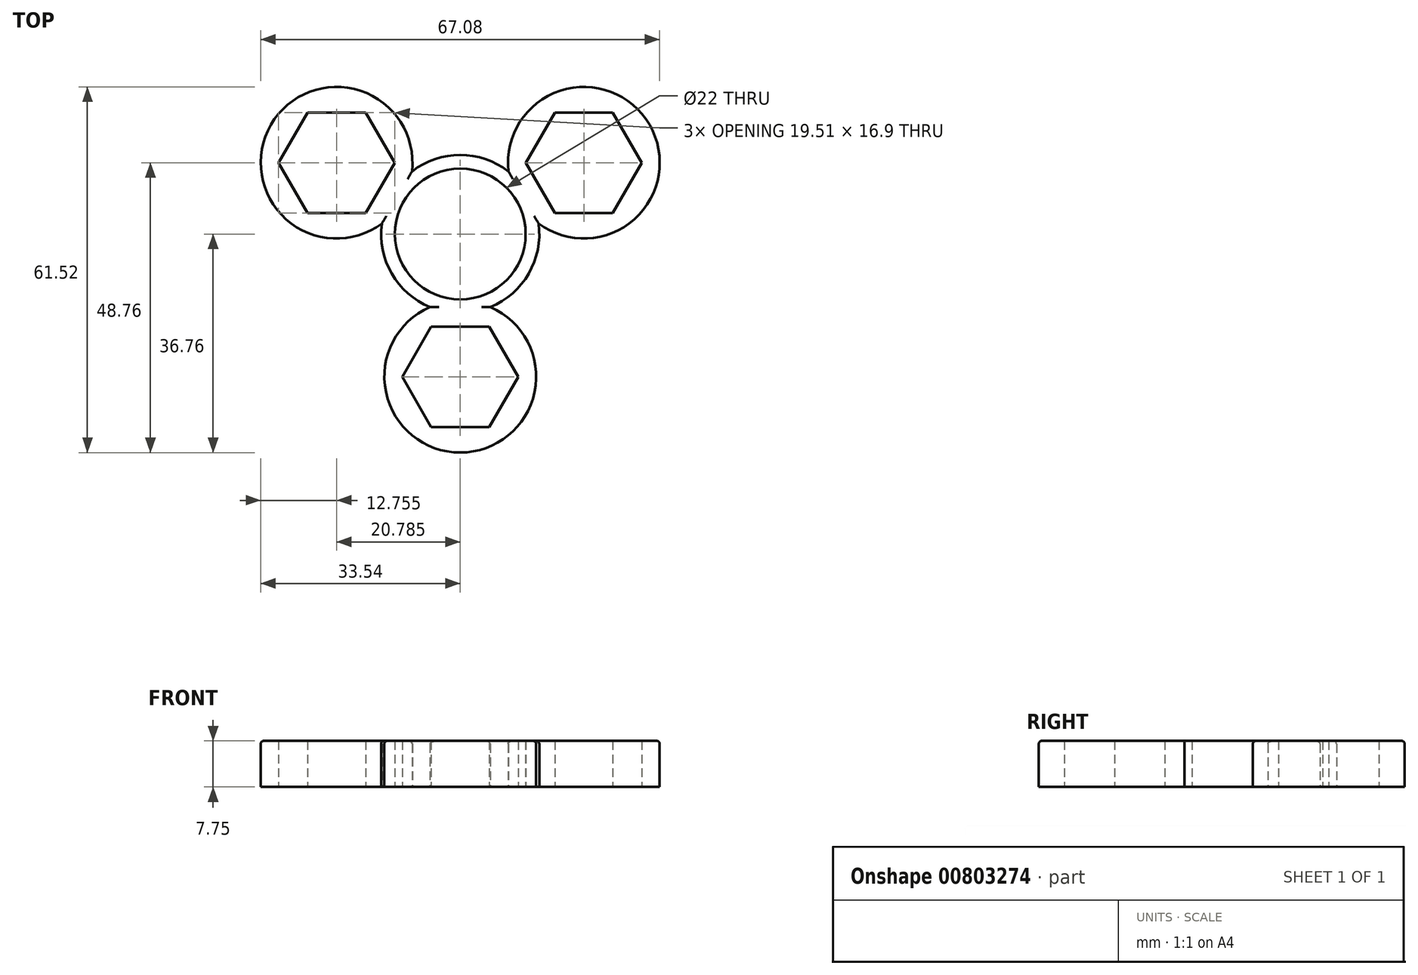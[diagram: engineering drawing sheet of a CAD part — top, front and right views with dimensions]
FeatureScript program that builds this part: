
annotation { "Feature Type Name" : "Feature", "Feature Type Description" : "" }
export const myFeature = defineFeature(function(context is Context, id is Id, definition is map)
    precondition{}
    {
        {
            var Q0;
            Q0=qCreatedBy(makeId("Top.planeOp"),FACE);
            var sketch = newSketch(context, id + "F0", { "sketchPlane" : qUnion([Q0])});
            skCircle(sketch, "E0", {"center": v(0, 0) * mm, "radius": 13.3 * mm});
            skCircle(sketch, "E1", {"center": v(0, -24) * mm, "radius": 12.76 * mm});
            skCircle(sketch, "E2", {"center": v(20.78, 12) * mm, "radius": 12.76 * mm});
            skCircle(sketch, "E3", {"center": v(-20.78, 12) * mm, "radius": 12.76 * mm});
            skLineSegment(sketch, "E4", {"start": v(-48.98, 58.94) * mm, "end": v(-57.64, 53.94) * mm, "construction": true});
            skLineSegment(sketch, "E5", {"start": v(-48.98, 58.94) * mm, "end": v(-48.98, 68.94) * mm, "construction": true});
            skLineSegment(sketch, "E6", {"start": v(-48.98, 58.94) * mm, "end": v(-40.32, 53.94) * mm, "construction": true});
            skCircle(sketch, "E7", {"center": v(-40.32, 53.94) * mm, "radius": 2.5 * mm});
            skCircle(sketch, "E8", {"center": v(-57.64, 53.94) * mm, "radius": 2.5 * mm});
            skCircle(sketch, "E9", {"center": v(-48.98, 68.94) * mm, "radius": 2.5 * mm});
            skCircle(sketch, "E10.cCircle", {"center": v(-48.98, 68.94) * mm, "radius": 1.68 * mm, "construction": true});
            skLineSegment(sketch, "E10.0", {"start": v(-47.05, 68.82) * mm, "end": v(-48.12, 67.2) * mm});
            skLineSegment(sketch, "E10.1", {"start": v(-48.12, 67.2) * mm, "end": v(-50.05, 67.33) * mm});
            skLineSegment(sketch, "E10.2", {"start": v(-50.05, 67.33) * mm, "end": v(-50.91, 69.06) * mm});
            skLineSegment(sketch, "E10.3", {"start": v(-50.91, 69.06) * mm, "end": v(-49.84, 70.68) * mm});
            skLineSegment(sketch, "E10.4", {"start": v(-49.84, 70.68) * mm, "end": v(-47.9, 70.55) * mm});
            skLineSegment(sketch, "E10.5", {"start": v(-47.9, 70.55) * mm, "end": v(-47.05, 68.82) * mm});
            skPoint(sketch, "E10.0.midPoint", {"position": v(-47.58, 68.01) * mm});
            skLineSegment(sketch, "E11", {"start": v(-20.78, 12) * mm, "end": v(0, 0) * mm, "construction": true});
            skLineSegment(sketch, "E12", {"start": v(20.78, 12) * mm, "end": v(0, 0) * mm, "construction": true});
            skLineSegment(sketch, "E13", {"start": v(0, -24) * mm, "end": v(0, 0) * mm, "construction": true});
            skCircle(sketch, "E14.cCircle", {"center": v(-20.78, 12) * mm, "radius": 8.45 * mm, "construction": true});
            skLineSegment(sketch, "E14.0", {"start": v(-25.66, 20.45) * mm, "end": v(-15.9, 20.45) * mm});
            skLineSegment(sketch, "E14.1", {"start": v(-15.9, 20.45) * mm, "end": v(-11.03, 12) * mm});
            skLineSegment(sketch, "E14.2", {"start": v(-11.03, 12) * mm, "end": v(-15.9, 3.55) * mm});
            skLineSegment(sketch, "E14.3", {"start": v(-15.9, 3.55) * mm, "end": v(-25.66, 3.55) * mm});
            skLineSegment(sketch, "E14.4", {"start": v(-25.66, 3.55) * mm, "end": v(-30.54, 12) * mm});
            skLineSegment(sketch, "E14.5", {"start": v(-30.54, 12) * mm, "end": v(-25.66, 20.45) * mm});
            skPoint(sketch, "E14.0.midPoint", {"position": v(-20.78, 20.45) * mm});
            skLineSegment(sketch, "E15.1.0", {"start": v(4.88, -32.45) * mm, "end": v(-4.88, -32.45) * mm});
            skLineSegment(sketch, "E15.1.1", {"start": v(-4.88, -32.45) * mm, "end": v(-9.76, -24) * mm});
            skLineSegment(sketch, "E15.1.2", {"start": v(-9.76, -24) * mm, "end": v(-4.88, -15.55) * mm});
            skLineSegment(sketch, "E15.1.3", {"start": v(-4.88, -15.55) * mm, "end": v(4.88, -15.55) * mm});
            skLineSegment(sketch, "E15.1.4", {"start": v(4.88, -15.55) * mm, "end": v(9.76, -24) * mm});
            skLineSegment(sketch, "E15.1.5", {"start": v(9.76, -24) * mm, "end": v(4.88, -32.45) * mm});
            skLineSegment(sketch, "E15.2.0", {"start": v(25.66, 20.45) * mm, "end": v(30.54, 12) * mm});
            skLineSegment(sketch, "E15.2.1", {"start": v(30.54, 12) * mm, "end": v(25.66, 3.55) * mm});
            skLineSegment(sketch, "E15.2.2", {"start": v(25.66, 3.55) * mm, "end": v(15.9, 3.55) * mm});
            skLineSegment(sketch, "E15.2.3", {"start": v(15.9, 3.55) * mm, "end": v(11.03, 12) * mm});
            skLineSegment(sketch, "E15.2.4", {"start": v(11.03, 12) * mm, "end": v(15.9, 20.45) * mm});
            skLineSegment(sketch, "E15.2.5", {"start": v(15.9, 20.45) * mm, "end": v(25.66, 20.45) * mm});
            skCircle(sketch, "E16", {"center": v(0, 0) * mm, "radius": 11 * mm});
            skSolve(sketch);
        }
        {
            var Q0;
            Q0=makeQuery(id+"F0.imprint","IMPRINT",FACE,{"disambiguationData":[TD([[makeQuery(id+"F0.imprint","IMPRINT",EDGE,{"derivedFrom":sQuery(id+"F0.wireOp",EDGE,"E14.0")}),1.0]])]});
            var Q1;
            Q1=makeQuery(id+"F0.imprint","IMPRINT",FACE,{"disambiguationData":[TD([[makeQuery(id+"F0.imprint","IMPRINT",EDGE,{"derivedFrom":sQuery(id+"F0.wireOp",EDGE,"E15.2.0")}),1.0]])]});
            var Q2;
            Q2=makeQuery(id+"F0.imprint","IMPRINT",FACE,{"disambiguationData":[TD([[makeQuery(id+"F0.imprint","IMPRINT",EDGE,{"derivedFrom":sQuery(id+"F0.wireOp",EDGE,"E15.1.0")}),1.0]])]});
            var Q3;
            {var subQ0=sQuery(id+"F0.wireOp",EDGE,"E3");var subQ1=sQuery(id+"F0.wireOp",EDGE,"E0");var subQ2=makeQuery(id+"F0.imprint","INTERSECT",VERTEX,{"disambiguationData":[OD(0.0)],"derivedFrom":[subQ1,subQ0]});Q3=makeQuery(id+"F0.imprint","IMPRINT",FACE,{"disambiguationData":[TD([[makeQuery(id+"F0.imprint","IMPRINT",EDGE,{"disambiguationData":[TD([[subQ2,-1.0]])],"derivedFrom":subQ1}),1.0]])]});}
            var Q4;
            {var subQ0=sQuery(id+"F0.wireOp",EDGE,"E1");var subQ1=sQuery(id+"F0.wireOp",EDGE,"E0");var subQ2=makeQuery(id+"F0.imprint","INTERSECT",VERTEX,{"disambiguationData":[OD(0.0)],"derivedFrom":[subQ1,subQ0]});Q4=makeQuery(id+"F0.imprint","IMPRINT",FACE,{"disambiguationData":[TD([[makeQuery(id+"F0.imprint","IMPRINT",EDGE,{"disambiguationData":[TD([[subQ2,-1.0]])],"derivedFrom":subQ1}),1.0]])]});}
            var Q5;
            Q5=makeQuery(id+"F0.imprint","IMPRINT",FACE,{"disambiguationData":[TD([[makeQuery(id+"F0.imprint","IMPRINT",EDGE,{"derivedFrom":sQuery(id+"F0.wireOp",EDGE,"E16")}),-1.0]])]});
            var Q6;
            {var subQ0=sQuery(id+"F0.wireOp",EDGE,"E2");var subQ1=sQuery(id+"F0.wireOp",EDGE,"E0");var subQ2=makeQuery(id+"F0.imprint","INTERSECT",VERTEX,{"disambiguationData":[OD(0.0)],"derivedFrom":[subQ1,subQ0]});Q6=makeQuery(id+"F0.imprint","IMPRINT",FACE,{"disambiguationData":[TD([[makeQuery(id+"F0.imprint","IMPRINT",EDGE,{"disambiguationData":[TD([[subQ2,1.0]])],"derivedFrom":subQ1}),1.0]])]});}
            extrude(context, id + "F1", {"entities" : qUnion([Q0, Q1, Q2, Q3, Q4, Q5, Q6]), "depth" : 7.75 * mm, "offsetDistance" : 25 * mm});
        }
        {
            var Q0;
            Q0=makeQuery(id+"F1.opExtrude","CAP_EDGE",EDGE,{"disambiguationData":[OSD([sQuery(id+"F0.wireOp",EDGE,"E1")])],"isStart":false});
            var Q1;
            Q1=makeQuery(id+"F1.opExtrude","CAP_EDGE",EDGE,{"disambiguationData":[OSD([sQuery(id+"F0.wireOp",EDGE,"E2")])],"isStart":false});
            var Q2;
            {var subQ0=sQuery(id+"F0.wireOp",EDGE,"E0");Q2=makeQuery(id+"F1.opExtrude","CAP_EDGE",EDGE,{"disambiguationData":[OSD([subQ0]),TDD([makeQuery(id+"F0.imprint","IMPRINT",EDGE,{"disambiguationData":[TD([[makeQuery(id+"F0.imprint","INTERSECT",VERTEX,{"disambiguationData":[OD(1.0)],"derivedFrom":[subQ0,sQuery(id+"F0.wireOp",EDGE,"E2")]}),1.0]])],"derivedFrom":subQ0})])],"isStart":false});}
            var Q3;
            {var subQ0=sQuery(id+"F0.wireOp",EDGE,"E0");Q3=makeQuery(id+"F1.opExtrude","CAP_EDGE",EDGE,{"disambiguationData":[OSD([subQ0]),TDD([makeQuery(id+"F0.imprint","IMPRINT",EDGE,{"disambiguationData":[TD([[makeQuery(id+"F0.imprint","INTERSECT",VERTEX,{"disambiguationData":[OD(0.0)],"derivedFrom":[subQ0,sQuery(id+"F0.wireOp",EDGE,"E2")]}),-1.0]])],"derivedFrom":subQ0})])],"isStart":false});}
            var Q4;
            Q4=makeQuery(id+"F1.opExtrude","CAP_EDGE",EDGE,{"disambiguationData":[OSD([sQuery(id+"F0.wireOp",EDGE,"E3")])],"isStart":false});
            var Q5;
            {var subQ0=sQuery(id+"F0.wireOp",EDGE,"E0");Q5=makeQuery(id+"F1.opExtrude","CAP_EDGE",EDGE,{"disambiguationData":[OSD([subQ0]),TDD([makeQuery(id+"F0.imprint","IMPRINT",EDGE,{"disambiguationData":[TD([[makeQuery(id+"F0.imprint","INTERSECT",VERTEX,{"disambiguationData":[OD(1.0)],"derivedFrom":[subQ0,sQuery(id+"F0.wireOp",EDGE,"E3")]}),-1.0]])],"derivedFrom":subQ0})])],"isStart":false});}
            fillet(context, id + "F2", {"entities" : qUnion([Q0, Q1, Q2, Q3, Q4, Q5]), "radius" : 0.5 * mm, "tangentPropagation" : true, "allowEdgeOverflow" : false});
        }
    });
